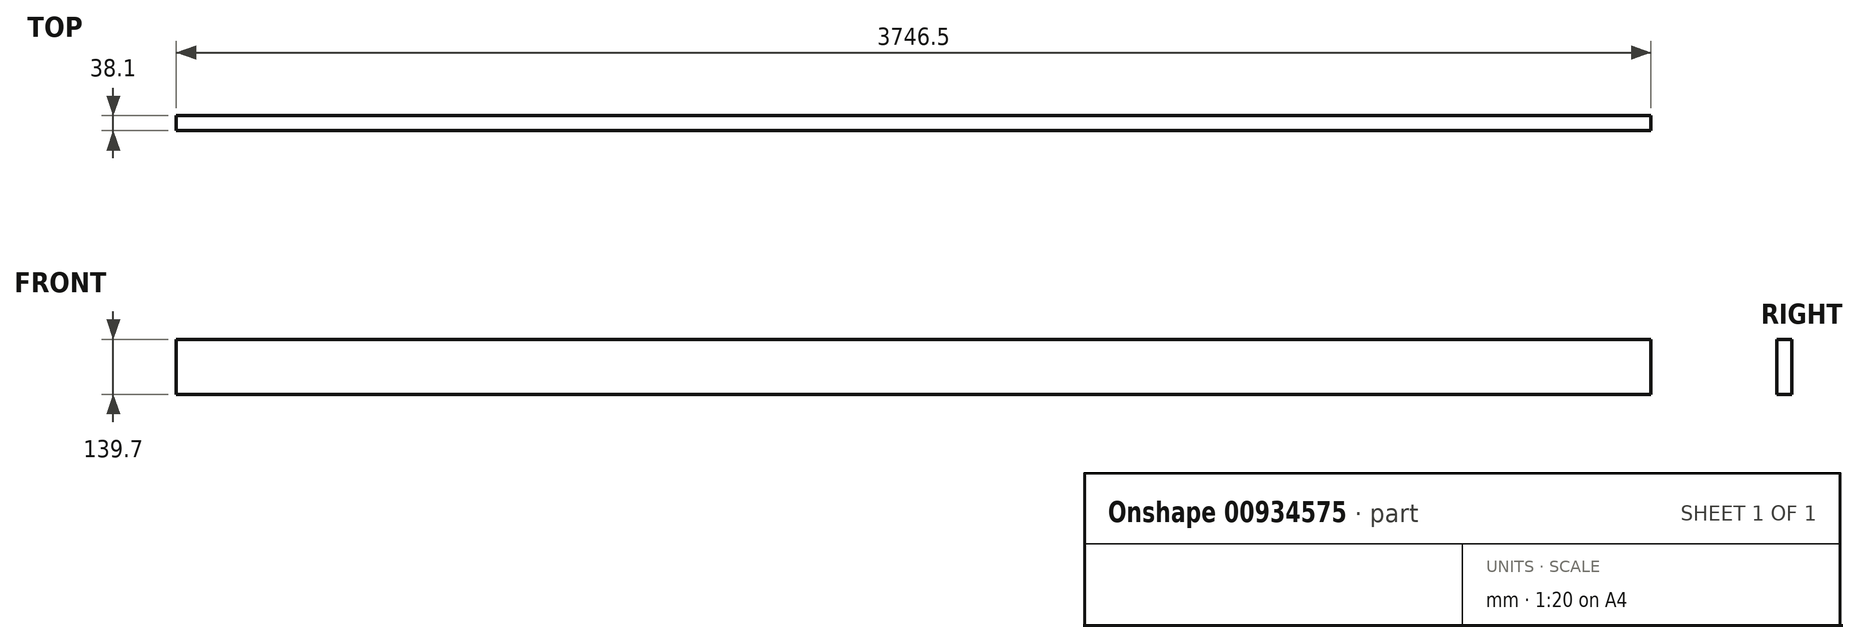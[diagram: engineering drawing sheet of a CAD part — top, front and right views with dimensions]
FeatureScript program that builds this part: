
annotation { "Feature Type Name" : "Feature", "Feature Type Description" : "" }
export const myFeature = defineFeature(function(context is Context, id is Id, definition is map)
    precondition{}
    {
        {
            var Q0;
            Q0=qCreatedBy(makeId("Front.planeOp"),FACE);
            var sketch = newSketch(context, id + "F0", { "sketchPlane" : qUnion([Q0])});
            skLineSegment(sketch, "E0.bottom", {"start": v(0, 0) * mm, "end": v(3746.5, 0) * mm});
            skLineSegment(sketch, "E0.top", {"start": v(0, 139.7) * mm, "end": v(3746.5, 139.7) * mm});
            skLineSegment(sketch, "E0.left", {"start": v(0, 0) * mm, "end": v(0, 139.7) * mm});
            skLineSegment(sketch, "E0.right", {"start": v(3746.5, 0) * mm, "end": v(3746.5, 139.7) * mm});
            skSolve(sketch);
        }
        {
            var Q0;
            Q0=makeQuery(id+"F0.imprint","IMPRINT",FACE,{"disambiguationData":[TD([[makeQuery(id+"F0.imprint","IMPRINT",EDGE,{"derivedFrom":sQuery(id+"F0.wireOp",EDGE,"E0.bottom")}),1.0]])]});
            extrude(context, id + "F1", {"entities" : qUnion([Q0]), "depth" : 38.1 * mm, "offsetDistance" : 25.4 * mm});
        }
    });
